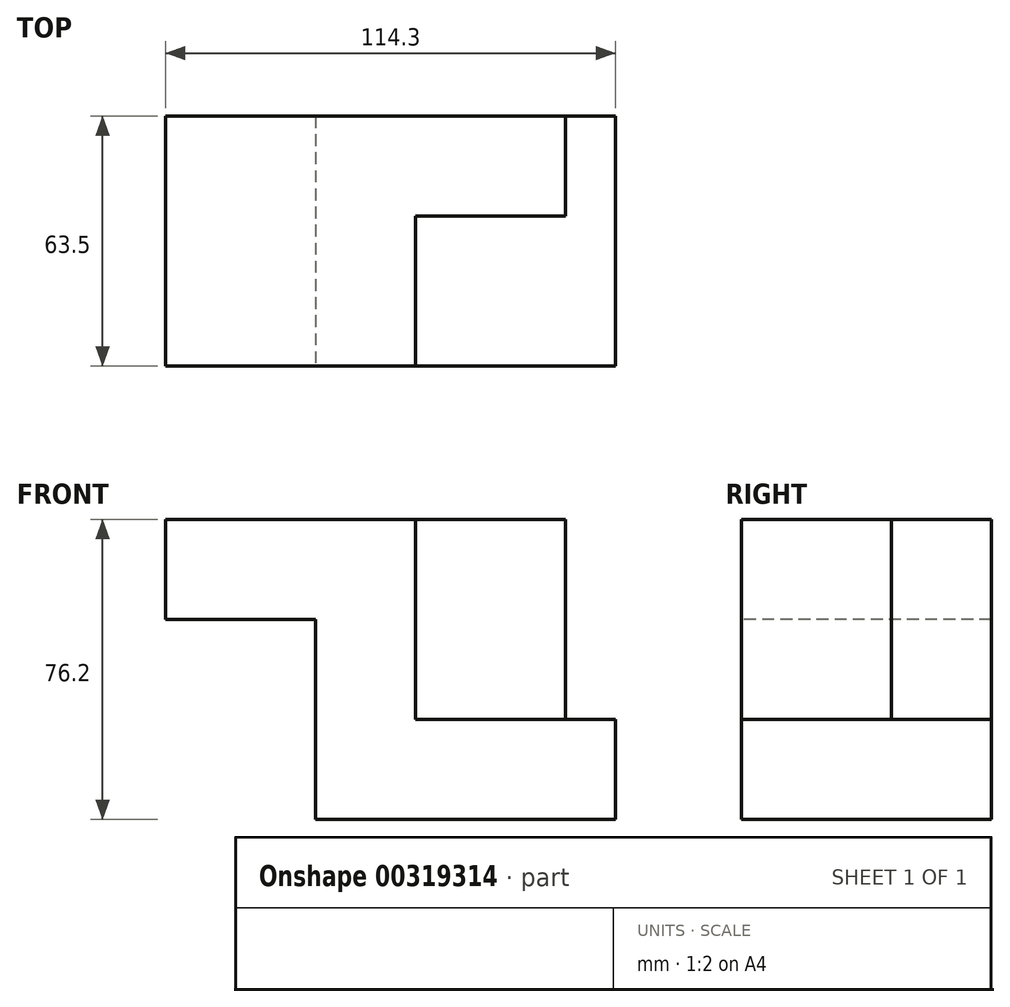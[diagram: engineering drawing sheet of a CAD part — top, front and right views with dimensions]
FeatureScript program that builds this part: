
annotation { "Feature Type Name" : "Feature", "Feature Type Description" : "" }
export const myFeature = defineFeature(function(context is Context, id is Id, definition is map)
    precondition{}
    {
        {
            var Q0;
            Q0=qCreatedBy(makeId("Top.planeOp"),FACE);
            var sketch = newSketch(context, id + "F0", { "sketchPlane" : qUnion([Q0])});
            skLineSegment(sketch, "E0", {"start": v(-54.2, -27.6) * mm, "end": v(22, -27.6) * mm});
            skLineSegment(sketch, "E1", {"start": v(22, -27.6) * mm, "end": v(22, 35.9) * mm});
            skLineSegment(sketch, "E2", {"start": v(22, 35.9) * mm, "end": v(-54.2, 35.9) * mm});
            skLineSegment(sketch, "E3", {"start": v(-54.2, 35.9) * mm, "end": v(-54.2, -27.6) * mm});
            skSolve(sketch);
        }
        {
            var Q0;
            Q0=makeQuery(id+"F0.imprint","IMPRINT",FACE,{"disambiguationData":[TD([[makeQuery(id+"F0.imprint","IMPRINT",EDGE,{"derivedFrom":sQuery(id+"F0.wireOp",EDGE,"E0")}),1.0]])]});
            extrude(context, id + "F1", {"entities" : qUnion([Q0]), "depth" : 25.4 * mm});
        }
        {
            var Q0;
            Q0=makeQuery(id+"F1.opExtrude","CAP_FACE",FACE,{"disambiguationData":[OSD([sQuery(id+"F0.wireOp",EDGE,"E0"),sQuery(id+"F0.wireOp",EDGE,"E1"),sQuery(id+"F0.wireOp",EDGE,"E2"),sQuery(id+"F0.wireOp",EDGE,"E3")])],"isStart":false});
            var sketch = newSketch(context, id + "F2", { "sketchPlane" : qUnion([Q0])});
            skLineSegment(sketch, "E4", {"start": v(-54.2, -27.6) * mm, "end": v(-28.8, -27.6) * mm});
            skLineSegment(sketch, "E5", {"start": v(-28.8, -27.6) * mm, "end": v(-28.8, 10.5) * mm});
            skLineSegment(sketch, "E6", {"start": v(-28.8, 10.5) * mm, "end": v(9.3, 10.5) * mm});
            skLineSegment(sketch, "E7", {"start": v(9.3, 10.5) * mm, "end": v(9.3, 35.9) * mm});
            skLineSegment(sketch, "E8", {"start": v(9.3, 35.9) * mm, "end": v(-54.2, 35.9) * mm});
            skLineSegment(sketch, "E9", {"start": v(-54.2, 35.9) * mm, "end": v(-54.2, -27.6) * mm});
            skSolve(sketch);
        }
        {
            var Q0;
            Q0=makeQuery(id+"F2.imprint","IMPRINT",FACE,{"disambiguationData":[TD([[makeQuery(id+"F2.imprint","IMPRINT",EDGE,{"derivedFrom":sQuery(id+"F2.wireOp",EDGE,"E4")}),1.0]])]});
            extrude(context, id + "F3", {"entities" : qUnion([Q0]), "operationType" : NewBodyOperationType.ADD, "depth" : 50.8 * mm});
        }
        {
            var Q0;
            Q0=makeQuery(id+"F3.boolean.opBoolean","MERGE",FACE,{"derivedFrom":[makeQuery(id+"F1.opExtrude","SWEPT_FACE",FACE,{"disambiguationData":[OSD([sQuery(id+"F0.wireOp",EDGE,"E3")])]}),makeQuery(id+"F3.opExtrude","SWEPT_FACE",FACE,{"disambiguationData":[OSD([sQuery(id+"F2.wireOp",EDGE,"E9")])]})]});
            var sketch = newSketch(context, id + "F4", { "sketchPlane" : qUnion([Q0])});
            skLineSegment(sketch, "E10", {"start": v(-35.9, 76.2) * mm, "end": v(-35.9, 50.8) * mm});
            skLineSegment(sketch, "E11", {"start": v(-35.9, 50.8) * mm, "end": v(27.6, 50.8) * mm});
            skLineSegment(sketch, "E12", {"start": v(27.6, 50.8) * mm, "end": v(27.6, 76.2) * mm});
            skLineSegment(sketch, "E13", {"start": v(27.6, 76.2) * mm, "end": v(-35.9, 76.2) * mm});
            skSolve(sketch);
        }
        {
            var Q0;
            Q0=makeQuery(id+"F4.imprint","IMPRINT",FACE,{"disambiguationData":[TD([[makeQuery(id+"F4.imprint","IMPRINT",EDGE,{"derivedFrom":sQuery(id+"F4.wireOp",EDGE,"E10")}),1.0]])]});
            extrude(context, id + "F5", {"entities" : qUnion([Q0]), "operationType" : NewBodyOperationType.ADD, "depth" : 38.1 * mm});
        }
    });
